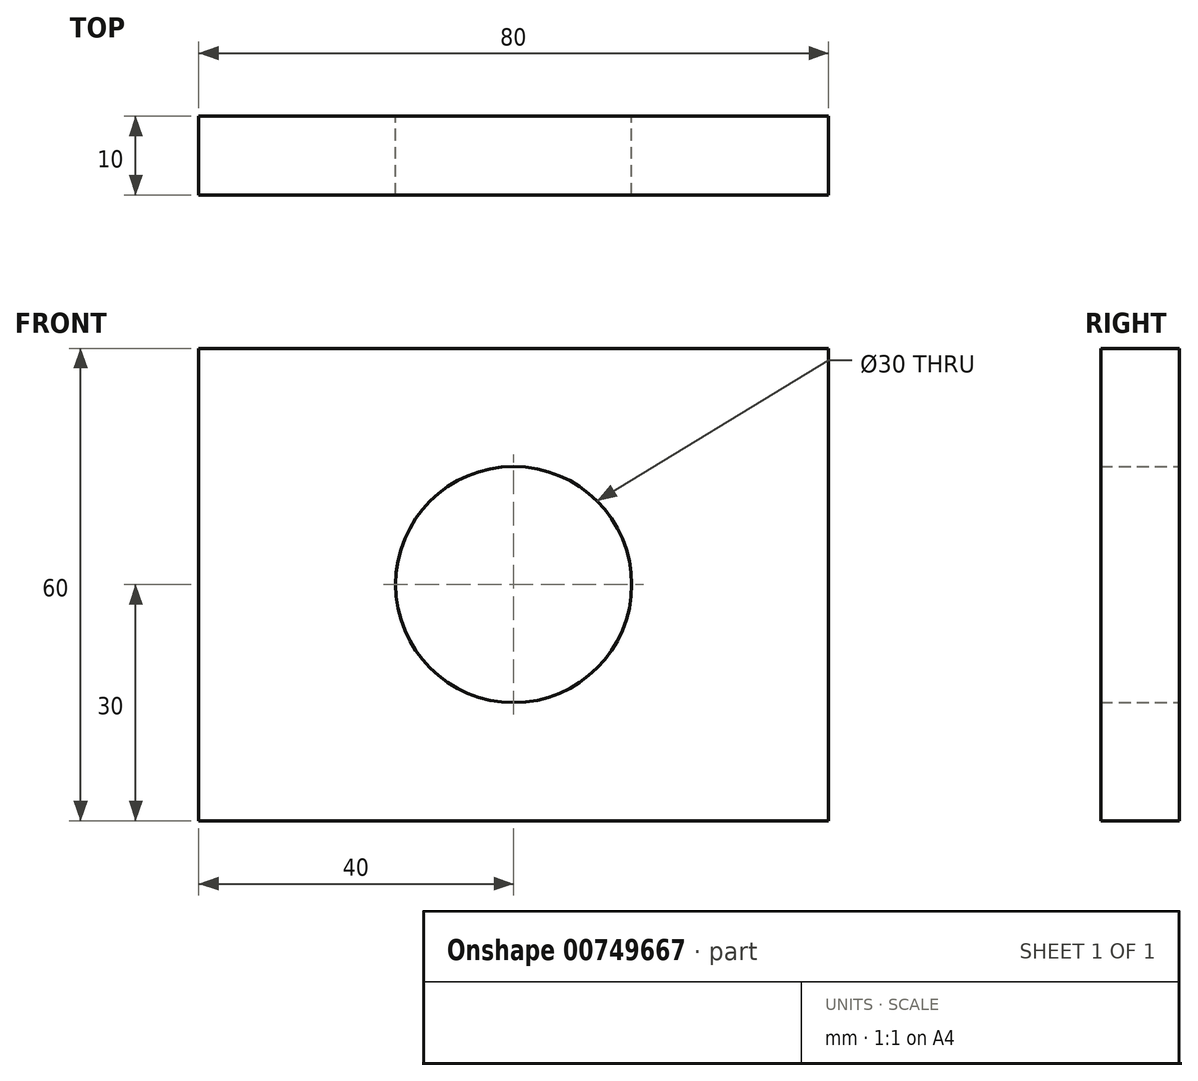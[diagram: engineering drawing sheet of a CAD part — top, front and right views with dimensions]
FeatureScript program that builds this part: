
annotation { "Feature Type Name" : "Feature", "Feature Type Description" : "" }
export const myFeature = defineFeature(function(context is Context, id is Id, definition is map)
    precondition{}
    {
        {
            var Q0;
            Q0=qCreatedBy(makeId("Front.planeOp"),FACE);
            var sketch = newSketch(context, id + "F0", { "sketchPlane" : qUnion([Q0])});
            skLineSegment(sketch, "E0.bottom", {"start": v(0, 0) * mm, "end": v(-80, 0) * mm});
            skLineSegment(sketch, "E0.top", {"start": v(0, 60) * mm, "end": v(-80, 60) * mm});
            skLineSegment(sketch, "E0.left", {"start": v(0, 0) * mm, "end": v(0, 60) * mm});
            skLineSegment(sketch, "E0.right", {"start": v(-80, 0) * mm, "end": v(-80, 60) * mm});
            skCircle(sketch, "E1", {"center": v(-40, 30) * mm, "radius": 15 * mm});
            skLineSegment(sketch, "E2", {"start": v(-40, 30) * mm, "end": v(0, 30) * mm, "construction": true});
            skLineSegment(sketch, "E3", {"start": v(-40, 30) * mm, "end": v(-80, 30) * mm, "construction": true});
            skSolve(sketch);
        }
        {
            var Q0;
            Q0 = qSketchRegion(id + "F0", true);
            extrude(context, id + "F1", {"entities" : qUnion([Q0]), "depth" : 10 * mm, "offsetDistance" : 25 * mm});
        }
    });
